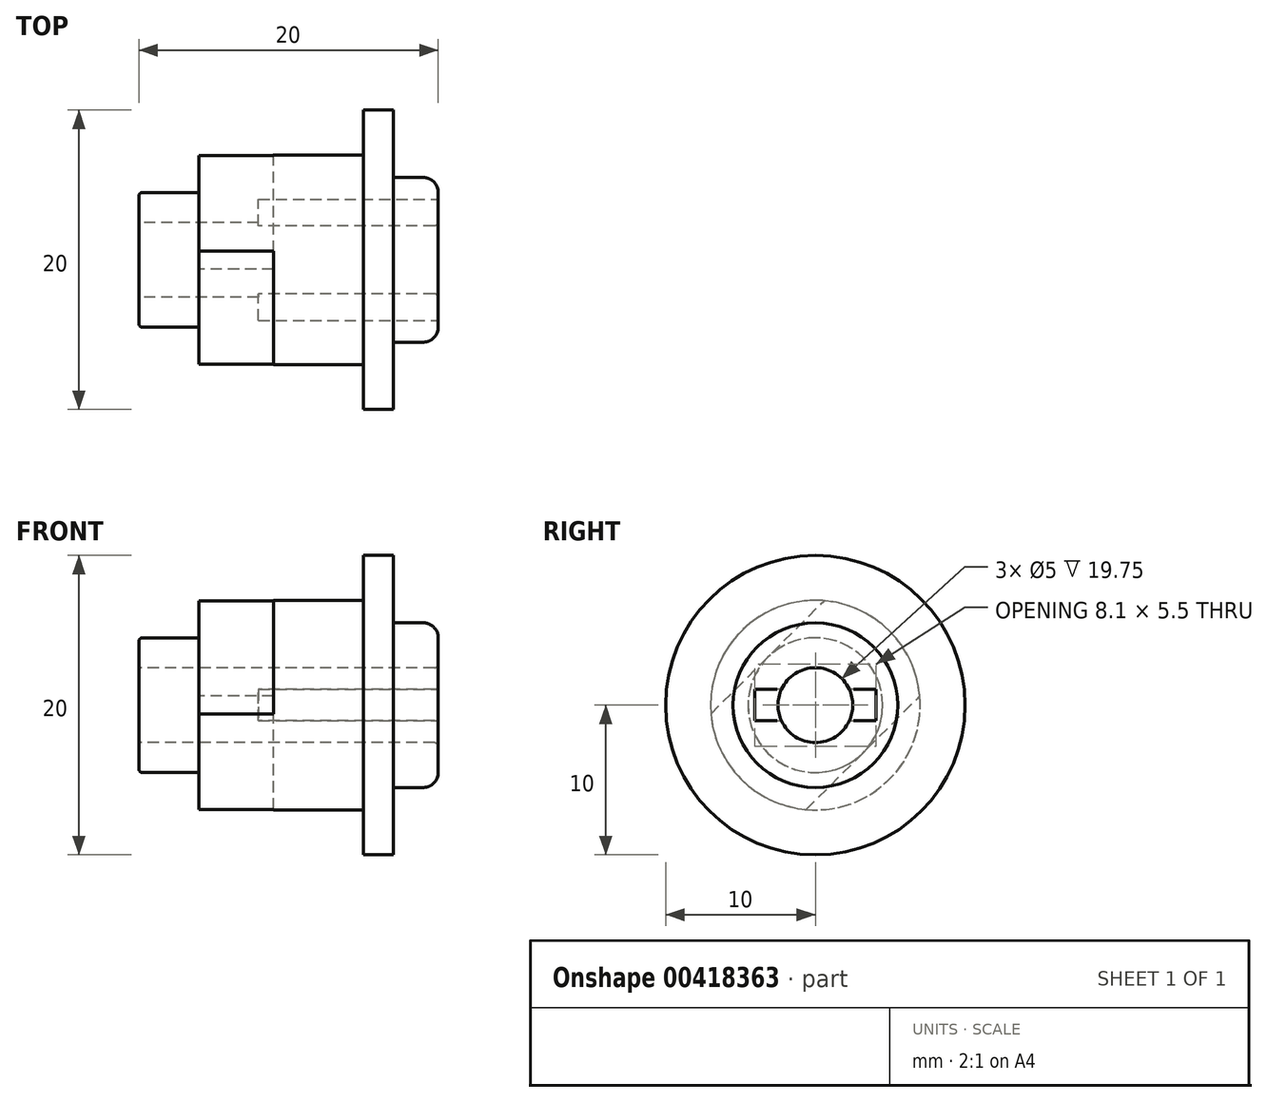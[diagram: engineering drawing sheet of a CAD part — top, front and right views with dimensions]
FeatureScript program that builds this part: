
annotation { "Feature Type Name" : "Feature", "Feature Type Description" : "" }
export const myFeature = defineFeature(function(context is Context, id is Id, definition is map)
    precondition{}
    {
        {
            var Q0;
            Q0=qCreatedBy(makeId("Front.planeOp"),FACE);
            var sketch = newSketch(context, id + "F0", { "sketchPlane" : qUnion([Q0]), "disableImprinting" : false});
            skLineSegment(sketch, "E0", {"start": v(-57.77, 0) * mm, "end": v(42.73, 0) * mm, "construction": true});
            skLineSegment(sketch, "E1", {"start": v(0, 2.5) * mm, "end": v(20, 2.5) * mm});
            skLineSegment(sketch, "E2", {"start": v(20, 2.5) * mm, "end": v(20, 5.5) * mm});
            skLineSegment(sketch, "E3", {"start": v(20, 5.5) * mm, "end": v(17, 5.5) * mm});
            skLineSegment(sketch, "E4", {"start": v(17, 5.5) * mm, "end": v(17, 10) * mm});
            skLineSegment(sketch, "E5", {"start": v(17, 10) * mm, "end": v(15, 10) * mm});
            skLineSegment(sketch, "E6", {"start": v(15, 10) * mm, "end": v(15, 7) * mm});
            skLineSegment(sketch, "E7", {"start": v(15, 7) * mm, "end": v(4, 7) * mm});
            skLineSegment(sketch, "E8", {"start": v(4, 7) * mm, "end": v(4, 4.5) * mm});
            skLineSegment(sketch, "E9", {"start": v(4, 4.5) * mm, "end": v(0, 4.5) * mm});
            skLineSegment(sketch, "E10", {"start": v(0, 4.5) * mm, "end": v(0, 2.5) * mm});
            skSolve(sketch);
        }
        {
            var Q0;
            Q0 = qSketchRegion(id + "F0", true);
            var Q1;
            Q1=sQuery(id+"F0.wireOp",EDGE,"E0");
            revolve(context, id + "F1", {"entities" : qUnion([Q0]), "axis" : qUnion([Q1]), "revolveType" : RevolveType.FULL});
        }
        {
            var Q0;
            Q0=makeQuery(id+"F1.opRevolve","SWEPT_EDGE",EDGE,{"disambiguationData":[OSD([sQuery(id+"F0.wireOp",EDGE,"E2"),sQuery(id+"F0.wireOp",EDGE,"E3")])]});
            fillet(context, id + "F2", {"entities" : qUnion([Q0]), "radius" : 1 * mm, "tangentPropagation" : true, "allowEdgeOverflow" : false});
        }
        {
            var Q0;
            Q0=makeQuery(id+"F1.opRevolve","SWEPT_FACE",FACE,{"disambiguationData":[OSD([sQuery(id+"F0.wireOp",EDGE,"E2")])]});
            var sketch = newSketch(context, id + "F3", { "sketchPlane" : qUnion([Q0])});
            skLineSegment(sketch, "E11.bottom", {"start": v(-4.05, -1.05) * mm, "end": v(4.05, -1.05) * mm});
            skLineSegment(sketch, "E11.top", {"start": v(-4.05, 1.05) * mm, "end": v(4.05, 1.05) * mm});
            skLineSegment(sketch, "E11.left", {"start": v(-4.05, -1.05) * mm, "end": v(-4.05, 1.05) * mm});
            skLineSegment(sketch, "E11.right", {"start": v(4.05, -1.05) * mm, "end": v(4.05, 1.05) * mm});
            skSolve(sketch);
        }
        {
            var Q0;
            Q0 = qSketchRegion(id + "F3", true);
            extrude(context, id + "F4", {"entities" : qUnion([Q0]), "operationType" : NewBodyOperationType.REMOVE, "depth" : 0 * mm, "hasSecondDirection" : true, "secondDirectionOppositeDirection" : true, "secondDirectionDepth" : 12 * mm});
        }
        {
            var Q0;
            {var subQ0=sQuery(id+"F3.wireOp",EDGE,"E11.bottom");Q0=makeQuery(id+"F4.boolean.opBoolean","COPY",EDGE,{"disambiguationData":[TD([makeQuery(id+"F4.opExtrude","SWEPT_FACE",FACE,{"disambiguationData":[OSD([sQuery(id+"F3.wireOp",EDGE,"E11.right")])]})])],"derivedFrom":makeQuery(id+"F4.opExtrude","CAP_EDGE",EDGE,{"disambiguationData":[OSD([subQ0])],"isStart":false})});}
            var Q1;
            Q1=makeQuery(id+"F4.boolean.opBoolean","COPY",EDGE,{"derivedFrom":makeQuery(id+"F4.opExtrude","CAP_EDGE",EDGE,{"disambiguationData":[OSD([sQuery(id+"F3.wireOp",EDGE,"E11.right")])],"isStart":false})});
            var Q2;
            {var subQ0=sQuery(id+"F3.wireOp",EDGE,"E11.top");Q2=makeQuery(id+"F4.boolean.opBoolean","COPY",EDGE,{"disambiguationData":[TD([makeQuery(id+"F4.opExtrude","SWEPT_FACE",FACE,{"disambiguationData":[OSD([sQuery(id+"F3.wireOp",EDGE,"E11.right")])]})])],"derivedFrom":makeQuery(id+"F4.opExtrude","CAP_EDGE",EDGE,{"disambiguationData":[OSD([subQ0])],"isStart":false})});}
            var Q3;
            {var subQ0=sQuery(id+"F0.wireOp",EDGE,"E1");var subQ1=sQuery(id+"F0.wireOp",EDGE,"E2");Q3=makeQuery(id+"F4.boolean.opBoolean","SPLIT",EDGE,{"disambiguationData":[TD([makeQuery(id+"F4.opExtrude","SWEPT_FACE",FACE,{"disambiguationData":[OSD([sQuery(id+"F3.wireOp",EDGE,"E11.top")])]})])],"derivedFrom":makeQuery(id+"F1.opRevolve","SWEPT_EDGE",EDGE,{"disambiguationData":[OSD([subQ0,subQ1])]})});}
            var Q4;
            {var subQ0=sQuery(id+"F0.wireOp",EDGE,"E1");var subQ1=sQuery(id+"F0.wireOp",EDGE,"E2");Q4=makeQuery(id+"F4.boolean.opBoolean","SPLIT",EDGE,{"disambiguationData":[TD([makeQuery(id+"F4.opExtrude","SWEPT_FACE",FACE,{"disambiguationData":[OSD([sQuery(id+"F3.wireOp",EDGE,"E11.bottom")])]})])],"derivedFrom":makeQuery(id+"F1.opRevolve","SWEPT_EDGE",EDGE,{"disambiguationData":[OSD([subQ0,subQ1])]})});}
            var Q5;
            {var subQ0=sQuery(id+"F3.wireOp",EDGE,"E11.bottom");Q5=makeQuery(id+"F4.boolean.opBoolean","COPY",EDGE,{"disambiguationData":[TD([makeQuery(id+"F4.opExtrude","SWEPT_FACE",FACE,{"disambiguationData":[OSD([sQuery(id+"F3.wireOp",EDGE,"E11.left")])]})])],"derivedFrom":makeQuery(id+"F4.opExtrude","CAP_EDGE",EDGE,{"disambiguationData":[OSD([subQ0])],"isStart":false})});}
            var Q6;
            {var subQ0=sQuery(id+"F3.wireOp",EDGE,"E11.top");Q6=makeQuery(id+"F4.boolean.opBoolean","COPY",EDGE,{"disambiguationData":[TD([makeQuery(id+"F4.opExtrude","SWEPT_FACE",FACE,{"disambiguationData":[OSD([sQuery(id+"F3.wireOp",EDGE,"E11.left")])]})])],"derivedFrom":makeQuery(id+"F4.opExtrude","CAP_EDGE",EDGE,{"disambiguationData":[OSD([subQ0])],"isStart":false})});}
            var Q7;
            Q7=makeQuery(id+"F4.boolean.opBoolean","COPY",EDGE,{"derivedFrom":makeQuery(id+"F4.opExtrude","CAP_EDGE",EDGE,{"disambiguationData":[OSD([sQuery(id+"F3.wireOp",EDGE,"E11.left")])],"isStart":false})});
            fillet(context, id + "F5", {"entities" : qUnion([Q0, Q1, Q2, Q3, Q4, Q5, Q6, Q7]), "radius" : 0.25 * mm, "tangentPropagation" : true, "allowEdgeOverflow" : false});
        }
        {
            var Q0;
            Q0=makeQuery(id+"F1.opRevolve","SWEPT_EDGE",EDGE,{"disambiguationData":[OSD([sQuery(id+"F0.wireOp",EDGE,"E9"),sQuery(id+"F0.wireOp",EDGE,"E10")])]});
            fillet(context, id + "F6", {"entities" : qUnion([Q0]), "radius" : 0.25 * mm, "tangentPropagation" : true, "allowEdgeOverflow" : false});
        }
        {
            var Q0;
            Q0=qCreatedBy(makeId("Right.planeOp"),FACE);
            var sketch = newSketch(context, id + "F7", { "sketchPlane" : qUnion([Q0])});
            skLineSegment(sketch, "E12.bottom", {"start": v(-0.73, -7.1) * mm, "end": v(7.05, 0.68) * mm});
            skLineSegment(sketch, "E12.top", {"start": v(1.04, -8.86) * mm, "end": v(8.82, -1.08) * mm});
            skLineSegment(sketch, "E12.left", {"start": v(-0.73, -7.1) * mm, "end": v(1.04, -8.86) * mm});
            skLineSegment(sketch, "E12.right", {"start": v(7.05, 0.68) * mm, "end": v(8.82, -1.08) * mm});
            skPoint(sketch, "E12.middle", {"position": v(-8.02, -15.67) * mm});
            skLineSegment(sketch, "E13.bottom", {"start": v(-8.9, 1.03) * mm, "end": v(-1.11, 8.8) * mm});
            skLineSegment(sketch, "E13.top", {"start": v(-7.13, -0.74) * mm, "end": v(0.65, 7.04) * mm});
            skLineSegment(sketch, "E13.left", {"start": v(-8.9, 1.03) * mm, "end": v(-7.13, -0.74) * mm});
            skLineSegment(sketch, "E13.right", {"start": v(-1.11, 8.8) * mm, "end": v(0.65, 7.04) * mm});
            skPoint(sketch, "E13.middle", {"position": v(-34.46, -41.55) * mm});
            skSolve(sketch);
        }
        {
            var Q0;
            Q0 = qSketchRegion(id + "F7", true);
            extrude(context, id + "F8", {"entities" : qUnion([Q0]), "operationType" : NewBodyOperationType.REMOVE, "oppositeDirection" : true, "depth" : 0.1 * mm, "hasSecondDirection" : true, "secondDirectionOppositeDirection" : false, "secondDirectionDepth" : 9 * mm});
        }
    });
